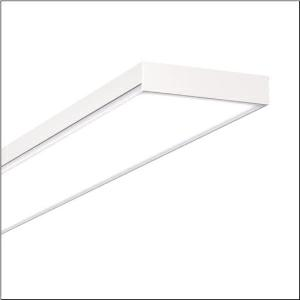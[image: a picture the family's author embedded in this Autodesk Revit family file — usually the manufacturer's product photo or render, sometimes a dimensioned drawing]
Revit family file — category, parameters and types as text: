
# Revit family: apollon_31_surface_51mp26wd2441wa
name_source: partatom
category: Lighting Fixtures
units: mm (PartAtom-declared; Revit-internal decimal feet)

## family parameters
Cut with Voids When Loaded = No
Host = Face
Light Source = No
Part Type = Normal
Room Calculation Point = No
Round Connector Dimension = Use Diameter
Shared = No

## types (1)
- Apollon 31 Surface (1 x LED, 4600 lm, 33 W, 4000K)
    Apparent Load = 33 VA
    CIE Flux Codes = 61 87 97 97 100
    Color Rendering = 80
    Color Temperature = 4000K
    Default Elevation = 1800 mm
    Description = Apollon 31 Surface, office luminaire, primary optical cover: micro prismatic cover, of PMMA, light emission: direct distribution, primary light characteristic: symmetric, installation type: surface-mounted, LED, rated luminous flux: 4.600lm, luminous efficacy: 139lm/W, light colour: 840, colour temperature: 4000K, control gear: DALI 2, with terminal, 5-pole, mains connection: 220..240V, AC, 50/60Hz, rated input power: 33W, housing, of sheet steel, coated, traffic white (RAL 9016), length: 1.545mm, width: 200mm, height: 44mm, protection rating (complete): IP20, protection rating (on room side): IP40, protection rating (lamp compartment, on room side): IP40, insulation class (complete): insulation class I (protective earthing), certification: CE, ENEC, UKCA, impact resistance: IK02, permissible operating ambient temperature: -20..+40°C, standard: EN 60598-2-22, packaging unit: 1 piece
    Height = 44 mm
    Lamp = 1 x LED
    Lamp Light Flux = 4600 lm
    Lamp Power = 33 W
    Lamp count = 1
    Length = 1545 mm
    Luminous efficacy = 139 lm/W
    Manufacturer = Siteco
    ModVariant = No
    Model = 51MP26WD2441WA
    Mounting Place = Ceiling
    Mounting Type = Surface mounted
    Number of Poles = 1
    OnlyDefault = Yes
    Power Factor = 1
    Product Name = Apollon 31 Surface
    Product group = office luminaire | ceiling mounted
    ProductGroupID = 301
    Protection Class = Protection class I
    Protection Degree = IP 20
    RLX_Detail_Level = 1
    RLX_Emergency_Light_Flux = 0 lm
    RLX_Emergency_Type = 0
    RLX_Emergency_Type_DB = No
    RlxData = <blob elided: 20825 chars, md5=b7c8d7d8>
    Socket = socket
    Standby Power = 0 W
    System Light Flux = 4600 lm
    System Power = 33 W
    Type Comments = Product without accessories
    Type Image = l_1313658.jpg
    URL = http://relux.com
    VarID = ---
    Voltage = 0 V
    Weight = 0.00 kg
    Width = 200 mm  [stored 0.656168 ft]

note: [stored X ft] marks values corroborated as IEEE doubles in the binary element streams (Revit-internal decimal feet)

## geometry (parser evidence)
native form markers: Blend x4, Sweep x14
no freeform markers — native parametric forms only
